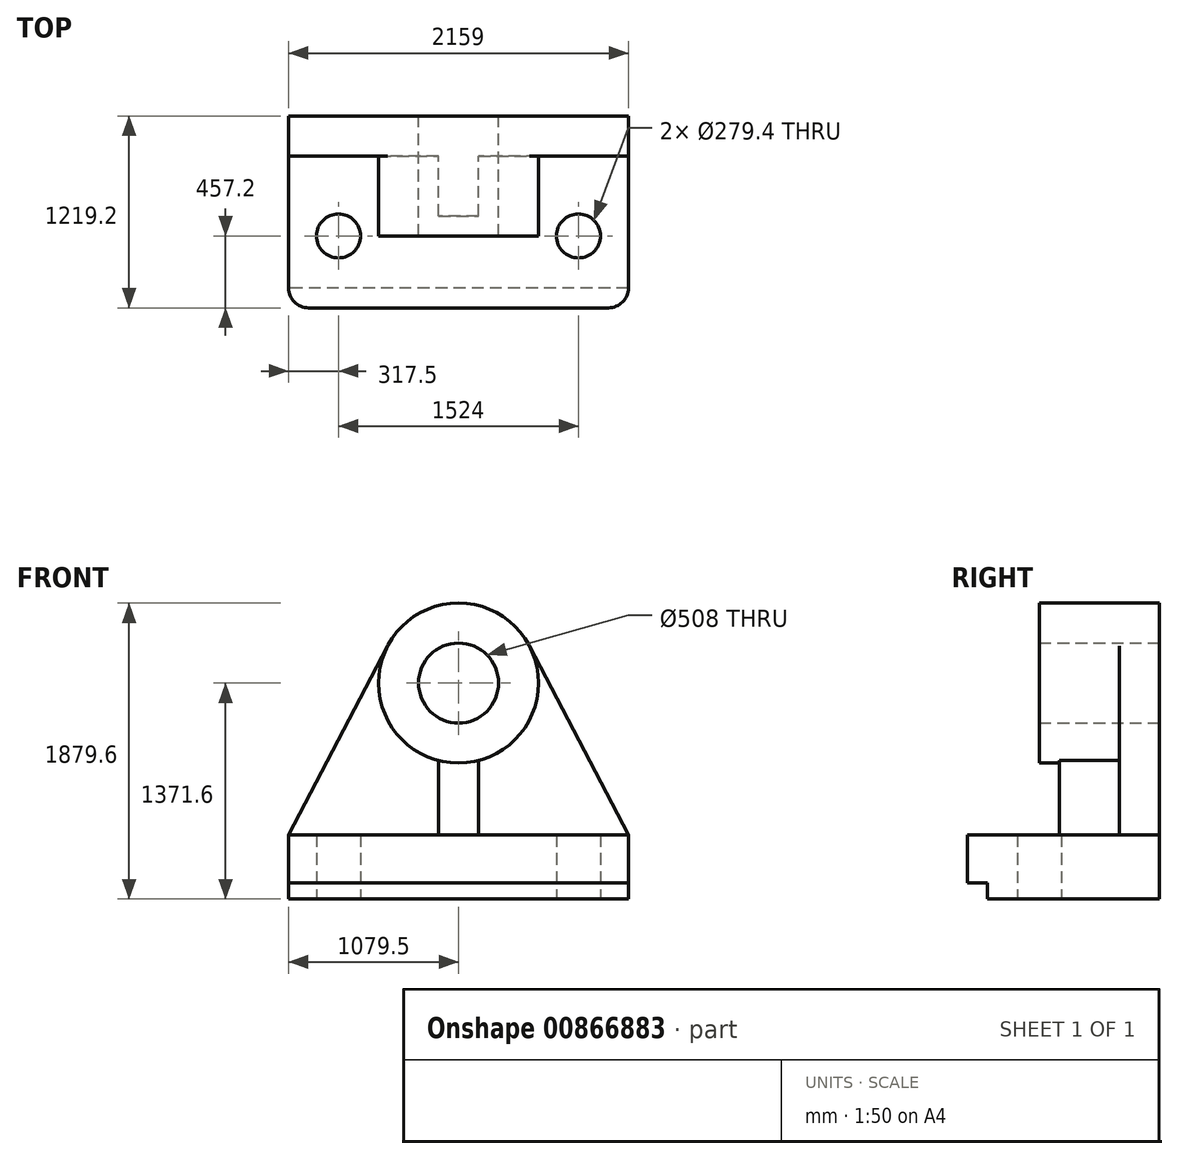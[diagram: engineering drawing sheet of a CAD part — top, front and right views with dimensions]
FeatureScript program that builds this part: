
annotation { "Feature Type Name" : "Feature", "Feature Type Description" : "" }
export const myFeature = defineFeature(function(context is Context, id is Id, definition is map)
    precondition{}
    {
        {
            var Q0;
            Q0=qCreatedBy(makeId("Top.planeOp"),FACE);
            var sketch = newSketch(context, id + "F0", { "sketchPlane" : qUnion([Q0])});
            skLineSegment(sketch, "E0.bottom", {"start": v(127, 0) * mm, "end": v(2032, 0) * mm});
            skLineSegment(sketch, "E0.top", {"start": v(0, 1219.2) * mm, "end": v(2159, 1219.2) * mm});
            skLineSegment(sketch, "E0.left", {"start": v(0, 127) * mm, "end": v(0, 1219.2) * mm});
            skLineSegment(sketch, "E0.right", {"start": v(2159, 127) * mm, "end": v(2159, 1219.2) * mm});
            skPoint(sketch, "E1.visualSharp", {"position": v(0, 0) * mm});
            skArc(sketch, "E1.filletArc", {"start": v(0, 127) * mm, "mid": v(37.2, 37.2) * mm, "end": v(127, 0) * mm});
            skPoint(sketch, "E2.visualSharp", {"position": v(2159, 0) * mm});
            skArc(sketch, "E2.filletArc", {"start": v(2032, 0) * mm, "mid": v(2121.8, 37.2) * mm, "end": v(2159, 127) * mm});
            skLineSegment(sketch, "E3", {"start": v(1079.5, 0) * mm, "end": v(1079.5, 457.2) * mm});
            skLineSegment(sketch, "E4", {"start": v(1079.5, 457.2) * mm, "end": v(317.5, 457.2) * mm});
            skLineSegment(sketch, "E5", {"start": v(1079.5, 457.2) * mm, "end": v(1841.5, 457.2) * mm});
            skCircle(sketch, "E6", {"center": v(317.5, 457.2) * mm, "radius": 139.7 * mm});
            skCircle(sketch, "E7", {"center": v(1841.5, 457.2) * mm, "radius": 139.7 * mm});
            skSolve(sketch);
        }
        {
            var Q0;
            Q0=makeQuery(id+"F0.imprint","IMPRINT",FACE,{"disambiguationData":[TD([[makeQuery(id+"F0.imprint","IMPRINT",EDGE,{"derivedFrom":sQuery(id+"F0.wireOp",EDGE,"E0.top")}),-1.0]])]});
            extrude(context, id + "F1", {"entities" : qUnion([Q0]), "depth" : 406.4 * mm, "offsetDistance" : 25.4 * mm});
        }
        {
            var Q0;
            Q0=makeQuery(id+"F1.opExtrude","SWEPT_FACE",FACE,{"disambiguationData":[OSD([sQuery(id+"F0.wireOp",EDGE,"E0.left")])]});
            var sketch = newSketch(context, id + "F2", { "sketchPlane" : qUnion([Q0])});
            skLineSegment(sketch, "E8", {"start": v(-1219.2, 0) * mm, "end": v(-1016, 0) * mm});
            skLineSegment(sketch, "E9", {"start": v(-1016, 0) * mm, "end": v(-1016, 101.6) * mm});
            skLineSegment(sketch, "E10.bottom", {"start": v(-1016, 101.6) * mm, "end": v(0, 101.6) * mm});
            skLineSegment(sketch, "E10.top", {"start": v(-1016, 0) * mm, "end": v(0, 0) * mm});
            skLineSegment(sketch, "E10.left", {"start": v(-1016, 101.6) * mm, "end": v(-1016, 0) * mm});
            skLineSegment(sketch, "E10.right", {"start": v(0, 101.6) * mm, "end": v(0, 0) * mm});
            skSolve(sketch);
        }
        {
            var Q0;
            {var subQ0=sQuery(id+"F2.wireOp",EDGE,"E10.left");Q0=makeQuery(id+"F2.imprint","IMPRINT",FACE,{"disambiguationData":[TD([[makeQuery(id+"F2.imprint","IMPRINT",EDGE,{"derivedFrom":subQ0}),1.0]])]});}
            var Q1;
            {var subQ0=sQuery(id+"F2.wireOp",EDGE,"E10.right");Q1=makeQuery(id+"F2.imprint","IMPRINT",FACE,{"disambiguationData":[TD([[makeQuery(id+"F2.imprint","IMPRINT",EDGE,{"derivedFrom":subQ0}),-1.0]])]});}
            extrude(context, id + "F3", {"entities" : qUnion([Q0, Q1]), "operationType" : NewBodyOperationType.REMOVE, "endBound" : BoundingType.THROUGH_ALL, "oppositeDirection" : true, "depth" : 25.4 * mm, "offsetDistance" : 25.4 * mm});
        }
        {
            var Q0;
            Q0=makeQuery(id+"F1.opExtrude","SWEPT_FACE",FACE,{"disambiguationData":[OSD([sQuery(id+"F0.wireOp",EDGE,"E0.top")])]});
            var sketch = newSketch(context, id + "F4", { "sketchPlane" : qUnion([Q0])});
            skLineSegment(sketch, "E11", {"start": v(-1079.5, 0) * mm, "end": v(-1079.5, 1371.6) * mm});
            skCircle(sketch, "E12", {"center": v(-1079.5, 1371.6) * mm, "radius": 508 * mm});
            skCircle(sketch, "E13", {"center": v(-1079.5, 1371.6) * mm, "radius": 254 * mm});
            skLineSegment(sketch, "E14", {"start": v(-2159, 406.4) * mm, "end": v(-1529.43, 1607.45) * mm});
            skLineSegment(sketch, "E15", {"start": v(0, 406.4) * mm, "end": v(-629.57, 1607.45) * mm});
            skLineSegment(sketch, "E16.bottom", {"start": v(-952.5, 406.4) * mm, "end": v(-1206.5, 406.4) * mm});
            skLineSegment(sketch, "E16.top", {"start": v(-952.5, 965.2) * mm, "end": v(-1206.5, 965.2) * mm});
            skLineSegment(sketch, "E16.left", {"start": v(-952.5, 406.4) * mm, "end": v(-952.5, 965.2) * mm});
            skLineSegment(sketch, "E16.right", {"start": v(-1206.5, 406.4) * mm, "end": v(-1206.5, 965.2) * mm});
            skPoint(sketch, "E16.middle", {"position": v(-1079.5, 685.8) * mm});
            skSolve(sketch);
        }
        {
            var Q0;
            {var subQ0=sQuery(id+"F4.wireOp",EDGE,"E15");Q0=makeQuery(id+"F4.imprint","IMPRINT",FACE,{"disambiguationData":[TD([[makeQuery(id+"F4.imprint","IMPRINT",EDGE,{"derivedFrom":subQ0}),1.0]])]});}
            var Q1;
            {var subQ0=sQuery(id+"F4.wireOp",EDGE,"E14");Q1=makeQuery(id+"F4.imprint","IMPRINT",FACE,{"disambiguationData":[TD([[makeQuery(id+"F4.imprint","IMPRINT",EDGE,{"derivedFrom":subQ0}),-1.0]])]});}
            var Q2;
            Q2=makeQuery(id+"F4.imprint","IMPRINT",FACE,{"disambiguationData":[TD([[makeQuery(id+"F4.imprint","IMPRINT",EDGE,{"derivedFrom":sQuery(id+"F4.wireOp",EDGE,"E13")}),-1.0]])]});
            var Q3;
            {var subQ0=sQuery(id+"F4.wireOp",EDGE,"E16.bottom");var subQ1=sQuery(id+"F4.wireOp",EDGE,"E11");var subQ2=makeQuery(id+"F4.imprint","INTERSECT",VERTEX,{"derivedFrom":[subQ1,subQ0]});Q3=makeQuery(id+"F4.imprint","IMPRINT",FACE,{"disambiguationData":[TD([[makeQuery(id+"F4.imprint","IMPRINT",EDGE,{"disambiguationData":[TD([[subQ2,-1.0]])],"derivedFrom":subQ1}),-1.0]])]});}
            var Q4;
            {var subQ0=sQuery(id+"F4.wireOp",EDGE,"E16.top");var subQ1=sQuery(id+"F4.wireOp",EDGE,"E11");var subQ2=makeQuery(id+"F4.imprint","INTERSECT",VERTEX,{"derivedFrom":[subQ1,subQ0]});Q4=makeQuery(id+"F4.imprint","IMPRINT",FACE,{"disambiguationData":[TD([[makeQuery(id+"F4.imprint","IMPRINT",EDGE,{"disambiguationData":[TD([[subQ2,1.0]])],"derivedFrom":subQ1}),-1.0]])]});}
            var Q5;
            {var subQ0=sQuery(id+"F4.wireOp",EDGE,"E16.top");var subQ1=sQuery(id+"F4.wireOp",EDGE,"E11");var subQ2=makeQuery(id+"F4.imprint","INTERSECT",VERTEX,{"derivedFrom":[subQ1,subQ0]});Q5=makeQuery(id+"F4.imprint","IMPRINT",FACE,{"disambiguationData":[TD([[makeQuery(id+"F4.imprint","IMPRINT",EDGE,{"disambiguationData":[TD([[subQ2,1.0]])],"derivedFrom":subQ1}),1.0]])]});}
            var Q6;
            {var subQ0=sQuery(id+"F4.wireOp",EDGE,"E16.bottom");var subQ1=sQuery(id+"F4.wireOp",EDGE,"E11");var subQ2=makeQuery(id+"F4.imprint","INTERSECT",VERTEX,{"derivedFrom":[subQ1,subQ0]});Q6=makeQuery(id+"F4.imprint","IMPRINT",FACE,{"disambiguationData":[TD([[makeQuery(id+"F4.imprint","IMPRINT",EDGE,{"disambiguationData":[TD([[subQ2,-1.0]])],"derivedFrom":subQ1}),1.0]])]});}
            extrude(context, id + "F5", {"entities" : qUnion([Q0, Q1, Q2, Q3, Q4, Q5, Q6]), "operationType" : NewBodyOperationType.ADD, "oppositeDirection" : true, "depth" : 254 * mm, "offsetDistance" : 25.4 * mm});
        }
        {
            var Q0;
            {var subQ0=sQuery(id+"F4.wireOp",EDGE,"E16.bottom");var subQ1=sQuery(id+"F4.wireOp",EDGE,"E11");var subQ2=makeQuery(id+"F4.imprint","INTERSECT",VERTEX,{"derivedFrom":[subQ1,subQ0]});Q0=makeQuery(id+"F4.imprint","IMPRINT",FACE,{"disambiguationData":[TD([[makeQuery(id+"F4.imprint","IMPRINT",EDGE,{"disambiguationData":[TD([[subQ2,-1.0]])],"derivedFrom":subQ1}),1.0]])]});}
            var Q1;
            {var subQ0=sQuery(id+"F4.wireOp",EDGE,"E16.bottom");var subQ1=sQuery(id+"F4.wireOp",EDGE,"E11");var subQ2=makeQuery(id+"F4.imprint","INTERSECT",VERTEX,{"derivedFrom":[subQ1,subQ0]});Q1=makeQuery(id+"F4.imprint","IMPRINT",FACE,{"disambiguationData":[TD([[makeQuery(id+"F4.imprint","IMPRINT",EDGE,{"disambiguationData":[TD([[subQ2,-1.0]])],"derivedFrom":subQ1}),-1.0]])]});}
            extrude(context, id + "F6", {"entities" : qUnion([Q0, Q1]), "operationType" : NewBodyOperationType.ADD, "oppositeDirection" : true, "depth" : 635 * mm, "offsetDistance" : 25.4 * mm});
        }
        {
            var Q0;
            {var subQ0=sQuery(id+"F4.wireOp",EDGE,"E16.top");var subQ1=sQuery(id+"F4.wireOp",EDGE,"E11");var subQ2=makeQuery(id+"F4.imprint","INTERSECT",VERTEX,{"derivedFrom":[subQ1,subQ0]});Q0=makeQuery(id+"F4.imprint","IMPRINT",FACE,{"disambiguationData":[TD([[makeQuery(id+"F4.imprint","IMPRINT",EDGE,{"disambiguationData":[TD([[subQ2,1.0]])],"derivedFrom":subQ1}),1.0]])]});}
            var Q1;
            Q1=makeQuery(id+"F4.imprint","IMPRINT",FACE,{"disambiguationData":[TD([[makeQuery(id+"F4.imprint","IMPRINT",EDGE,{"derivedFrom":sQuery(id+"F4.wireOp",EDGE,"E13")}),-1.0]])]});
            var Q2;
            {var subQ0=sQuery(id+"F4.wireOp",EDGE,"E16.top");var subQ1=sQuery(id+"F4.wireOp",EDGE,"E11");var subQ2=makeQuery(id+"F4.imprint","INTERSECT",VERTEX,{"derivedFrom":[subQ1,subQ0]});Q2=makeQuery(id+"F4.imprint","IMPRINT",FACE,{"disambiguationData":[TD([[makeQuery(id+"F4.imprint","IMPRINT",EDGE,{"disambiguationData":[TD([[subQ2,1.0]])],"derivedFrom":subQ1}),-1.0]])]});}
            extrude(context, id + "F7", {"entities" : qUnion([Q0, Q1, Q2]), "operationType" : NewBodyOperationType.ADD, "oppositeDirection" : true, "depth" : 762 * mm, "offsetDistance" : 25.4 * mm});
        }
    });
